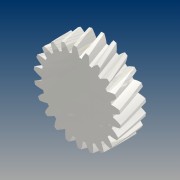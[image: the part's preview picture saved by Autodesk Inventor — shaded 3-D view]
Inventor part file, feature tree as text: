
AUTODESK INVENTOR PART (.ipt)
format: ipt  version: 2021 (Build 250183000, 183)  size: 477,184 bytes
history: native  units: mm (DEFAULTED — no unit token found)
features: extrude x3, plane x3, other x3, sketch x3
ambient origin geometry x8: Origin, YZ Plane, XZ Plane, XY Plane, X Axis, Y Axis, Z Axis, Center Point
bodies: Solid1 (feature_tree)
feature tree (12):
  extrude  "Extrusion1"  Depth=15.0mm TaperAngle=0.0deg
  plane  "Work Plane2"
  plane  "Work Plane8"
  plane  "Work Plane9"
  other  "Spur Gear"
  sketch  "Sketch3"  dims[d16=70.0mm d17=0.0mm d34=1.427997mm d39=0.0mm d41=0.0mm d43=70.0mm d46=70.0mm d47=0.0mm d48=0.0mm d49=10.0mm d50=5.0mm d51=0.0mm d52=0.0mm d53=10.0mm d54=0.0mm]
  extrude  "Extrusion2"  Depth=10.0mm TaperAngle=0.0deg
  extrude  "Extrusion3"  Depth=10.0mm TaperAngle=0.0deg
  sketch  "Sketch1"  dims[d0=50.766383mm d1=15.0mm d2=0.0mm]
  sketch  "Sketch2"  dims[d3=46.823822mm d4=10.0mm d5=0.0mm]
  other  "Srf1"
  other  "Pitch Diameter"
